# Revit family: ESS Twin
name_source: partatom
category: Mechanical Equipment
revit_build: Autodesk Revit 2015 (Build: 20160512_1515(x64)
units: mm (PartAtom-declared; Revit-internal decimal feet)

## types (1)
- ESS - Twin
    Central Heating Return = 19 mm  [stored 0.062336 ft]
    Central Heating Supply = 19 mm  [stored 0.062336 ft]
    Connections = ¾” BSP Insulated Pipe
    Domestic Cold Water Inlet = 19 mm  [stored 0.062336 ft]
    Domestic Cold Water Outlet = 19 mm  [stored 0.062336 ft]
    Domestic Hot Water = 19 mm  [stored 0.062336 ft]
    Heat transfer capacity = 5-70kW
    Load Classification = Other
    Manufacturer = Essco Controls Ltd
    Max working pressure primary = 10 Bar
    Max working pressure secondary(heating) = 3 Bar
    Max working temperature = 95 °C
    Min working pressure DHW = 2 Bar
    Space Heating Return = 19 mm  [stored 0.062336 ft]
    Space Heating Supply = 19 mm  [stored 0.062336 ft]
    URL = www.esscocontrols.co.uk
    Voltage = 240 V

note: [stored X ft] marks values corroborated as IEEE doubles in the binary element streams (Revit-internal decimal feet)

## geometry (parser evidence)
native form markers: Sweep x20
no freeform markers — native parametric forms only
